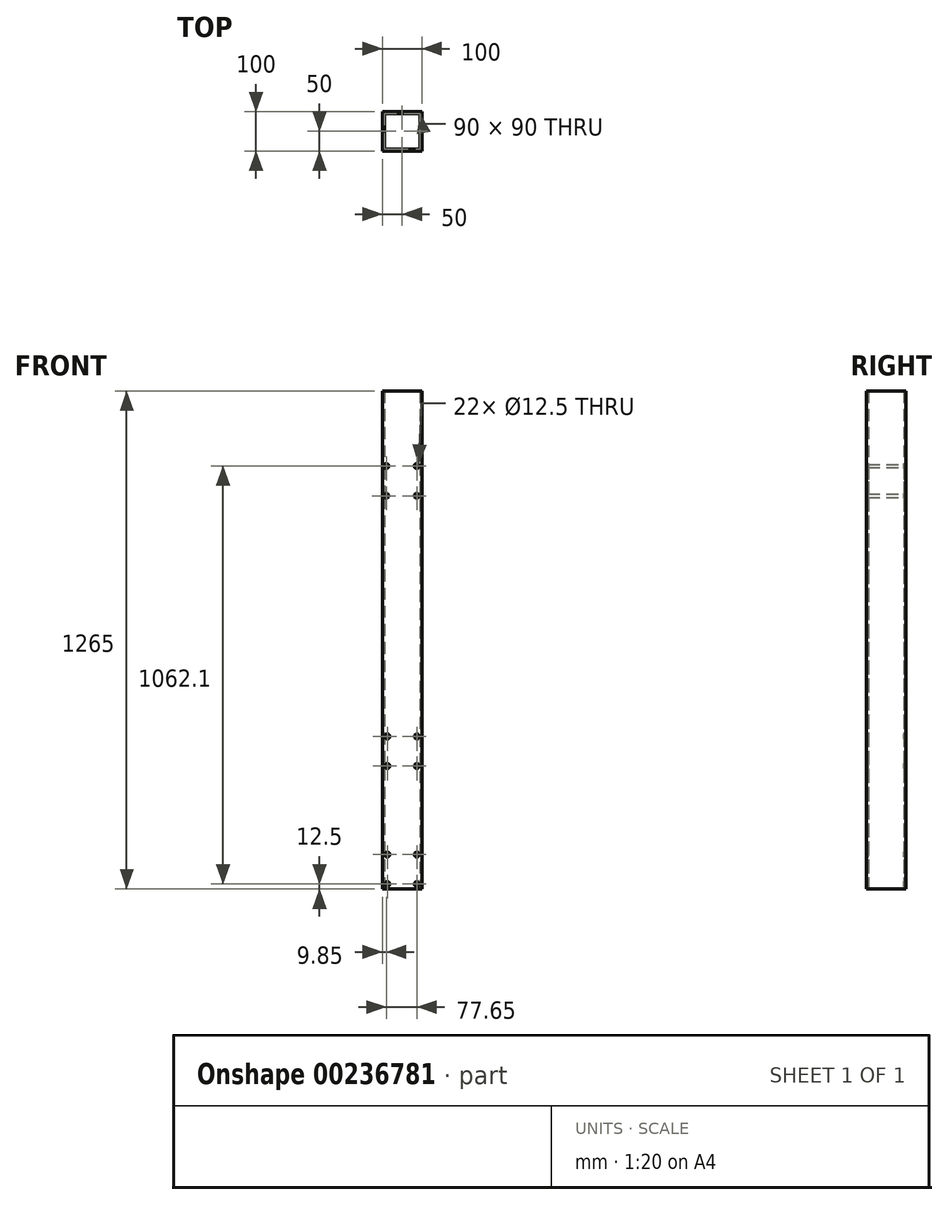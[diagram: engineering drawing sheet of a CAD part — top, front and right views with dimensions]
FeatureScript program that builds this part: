
annotation { "Feature Type Name" : "Feature", "Feature Type Description" : "" }
export const myFeature = defineFeature(function(context is Context, id is Id, definition is map)
    precondition{}
    {
        {
            var Q0;
            Q0=qCreatedBy(makeId("Top.planeOp"),FACE);
            var sketch = newSketch(context, id + "F0", { "sketchPlane" : qUnion([Q0])});
            skLineSegment(sketch, "E0.bottom", {"start": v(50, 50) * mm, "end": v(-50, 50) * mm});
            skLineSegment(sketch, "E0.top", {"start": v(50, -50) * mm, "end": v(-50, -50) * mm});
            skLineSegment(sketch, "E0.left", {"start": v(50, 50) * mm, "end": v(50, -50) * mm});
            skLineSegment(sketch, "E0.right", {"start": v(-50, 50) * mm, "end": v(-50, -50) * mm});
            skPoint(sketch, "E0.middle", {"position": v(0, 0) * mm});
            skLineSegment(sketch, "E1.bottom", {"start": v(45, 45) * mm, "end": v(-45, 45) * mm});
            skLineSegment(sketch, "E1.top", {"start": v(45, -45) * mm, "end": v(-45, -45) * mm});
            skLineSegment(sketch, "E1.left", {"start": v(45, 45) * mm, "end": v(45, -45) * mm});
            skLineSegment(sketch, "E1.right", {"start": v(-45, 45) * mm, "end": v(-45, -45) * mm});
            skSolve(sketch);
        }
        {
            var Q0;
            Q0 = qSketchRegion(id + "F0", true);
            extrude(context, id + "F1", {"entities" : qUnion([Q0]), "depth" : 1265 * mm, "offsetDistance" : 25 * mm});
        }
        {
            var Q0;
            Q0=makeQuery(id+"F1.opExtrude","SWEPT_FACE",FACE,{"disambiguationData":[OSD([sQuery(id+"F0.wireOp",EDGE,"E0.top")])]});
            var sketch = newSketch(context, id + "F2", { "sketchPlane" : qUnion([Q0])});
            skPoint(sketch, "E2", {"position": v(-37.5, 12.5) * mm});
            skPoint(sketch, "E3", {"position": v(37.5, 12.5) * mm});
            skPoint(sketch, "E4", {"position": v(37.5, 87.5) * mm});
            skPoint(sketch, "E5", {"position": v(-37.5, 87.5) * mm});
            skPoint(sketch, "E6", {"position": v(-37.5, 312.5) * mm});
            skPoint(sketch, "E7", {"position": v(-37.5, 387.5) * mm});
            skPoint(sketch, "E8", {"position": v(37.5, 387.5) * mm});
            skPoint(sketch, "E9", {"position": v(37.5, 312.5) * mm});
            skSolve(sketch);
        }
        {
            var Q0;
            Q0=sQuery(id+"F2.wireOp",VERTEX,"E7");
            var Q1;
            Q1=sQuery(id+"F2.wireOp",VERTEX,"E8");
            var Q2;
            Q2=sQuery(id+"F2.wireOp",VERTEX,"E9");
            var Q3;
            Q3=sQuery(id+"F2.wireOp",VERTEX,"E6");
            var Q4;
            Q4=sQuery(id+"F2.wireOp",VERTEX,"E5");
            var Q5;
            Q5=sQuery(id+"F2.wireOp",VERTEX,"E2");
            var Q6;
            Q6=sQuery(id+"F2.wireOp",VERTEX,"E4");
            var Q7;
            Q7=sQuery(id+"F2.wireOp",VERTEX,"E3");
            var Q8;
            Q8=makeQuery(id+"F1.opExtrude","SWEPT_BODY",BODY,{"disambiguationData":[OSD([sQuery(id+"F0.wireOp",EDGE,"E0.bottom"),sQuery(id+"F0.wireOp",EDGE,"E0.top"),sQuery(id+"F0.wireOp",EDGE,"E0.left"),sQuery(id+"F0.wireOp",EDGE,"E0.right"),sQuery(id+"F0.wireOp",EDGE,"E1.bottom"),sQuery(id+"F0.wireOp",EDGE,"E1.top"),sQuery(id+"F0.wireOp",EDGE,"E1.left"),sQuery(id+"F0.wireOp",EDGE,"E1.right")])]});
            hole(context, id + "F3", {"style" : HoleStyle.SIMPLE, "endStyle" : HoleEndStyle.THROUGH, "holeDiameter" : 12.5 * mm, "majorDiameter" : 5 * mm, "isTappedThrough" : true, "tappedDepth" : 31.25 * mm, "tapClearance" : 3, "startFromSketch" : true, "locations" : qUnion([Q0, Q1, Q2, Q3, Q4, Q5, Q6, Q7]), "scope" : qUnion([Q8])});
        }
        {
            var Q0;
            Q0=makeQuery(id+"F1.opExtrude","SWEPT_FACE",FACE,{"disambiguationData":[OSD([sQuery(id+"F0.wireOp",EDGE,"E0.top")])]});
            var sketch = newSketch(context, id + "F4", { "sketchPlane" : qUnion([Q0])});
            skPoint(sketch, "E10", {"position": v(-40.15, 1074.6) * mm});
            skPoint(sketch, "E11", {"position": v(37.25, 1074.6) * mm});
            skPoint(sketch, "E12", {"position": v(37.25, 999.04) * mm});
            skPoint(sketch, "E13", {"position": v(-40.15, 999.04) * mm});
            skSolve(sketch);
        }
        {
            var Q0;
            Q0=sQuery(id+"F4.wireOp",VERTEX,"E13");
            var Q1;
            Q1=sQuery(id+"F4.wireOp",VERTEX,"E12");
            var Q2;
            Q2=sQuery(id+"F4.wireOp",VERTEX,"E10");
            var Q3;
            Q3=sQuery(id+"F4.wireOp",VERTEX,"E11");
            var Q4;
            Q4=makeQuery(id+"F1.opExtrude","SWEPT_BODY",BODY,{"disambiguationData":[OSD([sQuery(id+"F0.wireOp",EDGE,"E0.bottom"),sQuery(id+"F0.wireOp",EDGE,"E0.top"),sQuery(id+"F0.wireOp",EDGE,"E0.left"),sQuery(id+"F0.wireOp",EDGE,"E0.right"),sQuery(id+"F0.wireOp",EDGE,"E1.bottom"),sQuery(id+"F0.wireOp",EDGE,"E1.top"),sQuery(id+"F0.wireOp",EDGE,"E1.left"),sQuery(id+"F0.wireOp",EDGE,"E1.right")])]});
            hole(context, id + "F5", {"style" : HoleStyle.SIMPLE, "endStyle" : HoleEndStyle.THROUGH, "holeDiameter" : 12.5 * mm, "majorDiameter" : 5 * mm, "isTappedThrough" : true, "tappedDepth" : 31.25 * mm, "tapClearance" : 3, "startFromSketch" : true, "locations" : qUnion([Q0, Q1, Q2, Q3]), "scope" : qUnion([Q4])});
        }
    });
